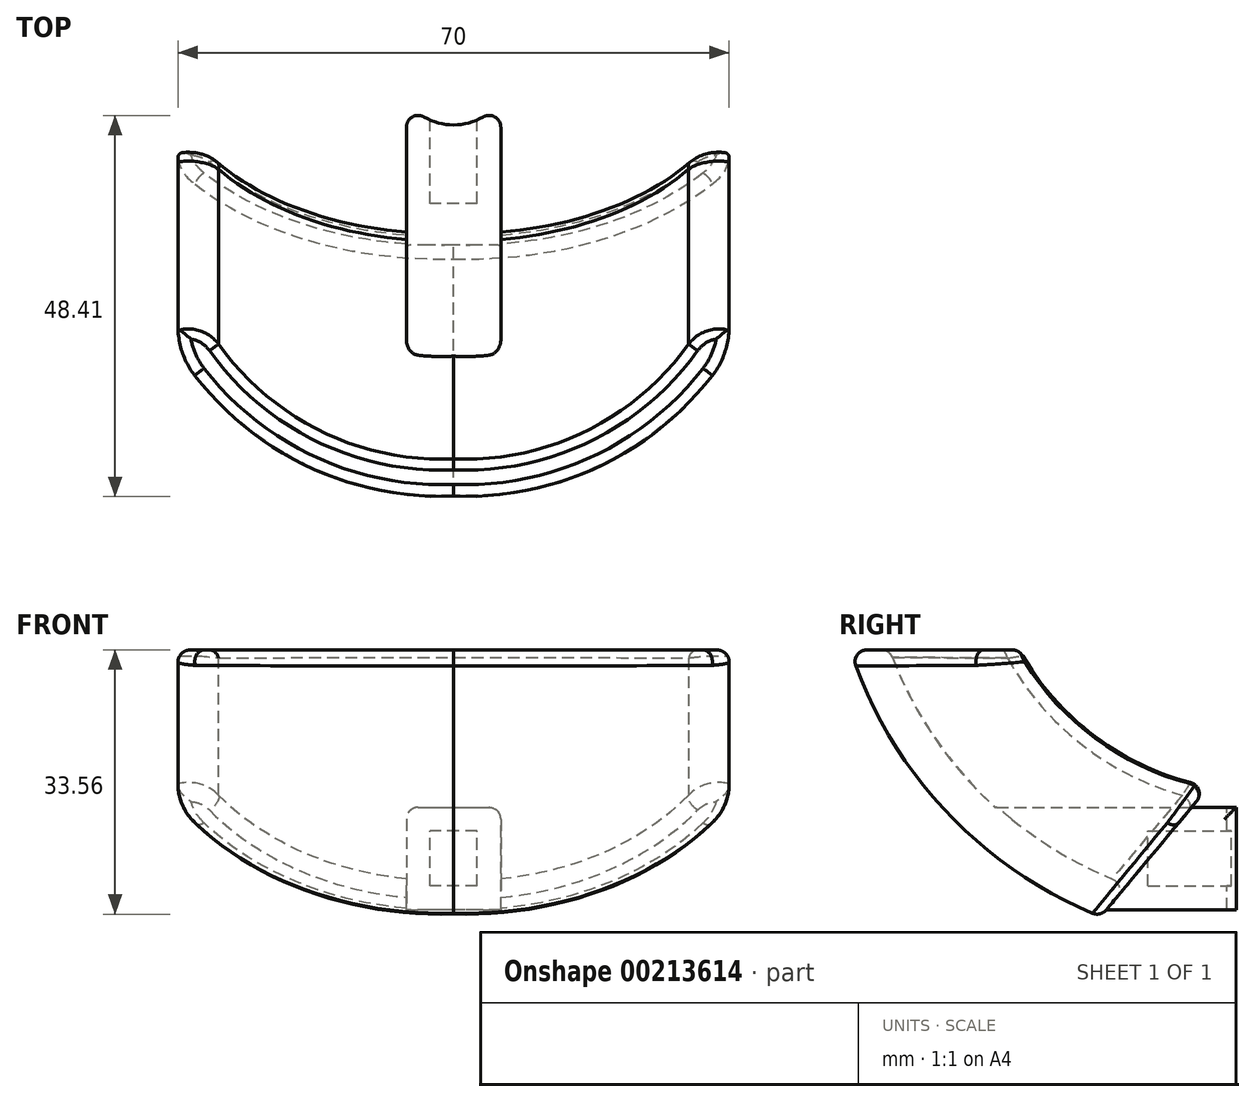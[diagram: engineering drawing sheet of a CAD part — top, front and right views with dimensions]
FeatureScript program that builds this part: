
annotation { "Feature Type Name" : "Feature", "Feature Type Description" : "" }
export const myFeature = defineFeature(function(context is Context, id is Id, definition is map)
    precondition{}
    {
        {
            var Q0;
            Q0=qCreatedBy(makeId("Right.planeOp"),FACE);
            var sketch = newSketch(context, id + "F0", { "sketchPlane" : qUnion([Q0])});
            skLineSegment(sketch, "E0.bottom", {"start": v(0, 0) * mm, "end": v(30, 0) * mm, "construction": true});
            skLineSegment(sketch, "E0.left", {"start": v(0, 0) * mm, "end": v(0, 30) * mm, "construction": true});
            skArc(sketch, "E1", {"start": v(0, 30) * mm, "mid": v(11.66, 11.66) * mm, "end": v(30, 0) * mm});
            skPoint(sketch, "E2", {"position": v(13.08, 10.3) * mm});
            skPoint(sketch, "E3", {"position": v(-15, 30) * mm});
            skPoint(sketch, "E4", {"position": v(3.08, 10.3) * mm});
            skPoint(sketch, "E5", {"position": v(30, 0) * mm});
            skPoint(sketch, "E6", {"position": v(25, 0) * mm});
            skFitSpline(sketch, "E7", {"points": [v(-15, 30) * mm, v(25, 0) * mm, v(100.66, 9.32) * mm], "startDerivative": vector(35.39, -77.1) * mm, "endDerivative": vector(150.07, 40.05) * mm});
            skSolve(sketch);
        }
        {
            var Q0;
            Q0=sQuery(id+"F0.wireOp",VERTEX,"E1.start");
            var Q1;
            Q1=qCreatedBy(makeId("Top.planeOp"),FACE);
            cPlane(context, id + "F1", {"entities" : qUnion([Q0, Q1]), "cplaneType" : CPlaneType.PLANE_POINT, "offset" : 25 * mm, "width" : 150 * mm, "height" : 150 * mm});
        }
        {
            var Q0;
            Q0=qCreatedBy(id+"F1.planeOp",FACE);
            var sketch = newSketch(context, id + "F2", { "sketchPlane" : qUnion([Q0])});
            skArc(sketch, "E8", {"start": v(-35, 24.67) * mm, "mid": v(-21.71, 6.36) * mm, "end": v(0, 0) * mm});
            skArc(sketch, "E9", {"start": v(0, 0) * mm, "mid": v(21.71, 6.36) * mm, "end": v(35, 24.67) * mm});
            skLineSegment(sketch, "E10", {"start": v(-35, 24.67) * mm, "end": v(-35, 16.25) * mm});
            skArc(sketch, "E11.0", {"start": v(0, -5) * mm, "mid": v(18.2, -1.4) * mm, "end": v(32.82, 10.02) * mm});
            skArc(sketch, "E11.1", {"start": v(-32.82, 10.02) * mm, "mid": v(-18.2, -1.4) * mm, "end": v(0, -5) * mm});
            skLineSegment(sketch, "E12", {"start": v(35, 24.67) * mm, "end": v(35, 16.25) * mm});
            skEllipticalArc(sketch, "E13", {});
            skPoint(sketch, "E14.visualSharp", {"position": v(-35, 13.03) * mm});
            skArc(sketch, "E14.filletArc", {"start": v(-35, 16.25) * mm, "mid": v(-34.44, 12.95) * mm, "end": v(-32.82, 10.02) * mm});
            skPoint(sketch, "E15.visualSharp", {"position": v(35, 13.03) * mm});
            skArc(sketch, "E15.filletArc", {"start": v(32.82, 10.02) * mm, "mid": v(34.44, 12.95) * mm, "end": v(35, 16.25) * mm});
            skEllipticalArc(sketch, "E16.trimOffspring", {});
            skPoint(sketch, "E17.orphan", {"position": v(0, -15) * mm});
            const initialGuessF2  = {"E13": [0, -0.005004295268239853, 0, -1, 0.01, 0.00424685629998106, 4.184836836168355, 4.7062911756630585], "E16.trimOffspring": [0, -0.005004295268239853, 0, -1, 0.01, 0.00424685629998106, 1.576894131516556, 2.098348471011326]};
            skSetInitialGuess(sketch, initialGuessF2);
            skSolve(sketch);
        }
        {
            var Q0;
            Q0=sQuery(id+"F0.wireOp",VERTEX,"E2");
            var Q1;
            Q1=qCreatedBy(makeId("Top.planeOp"),FACE);
            cPlane(context, id + "F3", {"entities" : qUnion([Q0, Q1]), "cplaneType" : CPlaneType.PLANE_POINT, "offset" : 25 * mm, "width" : 150 * mm, "height" : 150 * mm});
        }
        {
            var Q0;
            {var subQ5=sQuery(id+"F2.wireOp",EDGE,"E10");Q0=makeQuery(id+"F2.imprint","IMPRINT",FACE,{"disambiguationData":[TD([[makeQuery(id+"F2.imprint","IMPRINT",EDGE,{"derivedFrom":subQ5}),1.0]])]});}
            var Q1;
            {var subQ6=sQuery(id+"F2.wireOp",EDGE,"E9");var subQ7=sQuery(id+"F2.wireOp",EDGE,"E8");var subQ8=makeQuery(id+"F2.imprint","INTERSECT",VERTEX,{"derivedFrom":[subQ7,subQ6]});Q1=makeQuery(id+"F2.imprint","IMPRINT",FACE,{"disambiguationData":[TD([[makeQuery(id+"F2.imprint","IMPRINT",EDGE,{"disambiguationData":[TD([[subQ8,1.0]])],"derivedFrom":subQ7}),-1.0]])]});}
            var Q2;
            {var subQ5=sQuery(id+"F2.wireOp",EDGE,"E12");Q2=makeQuery(id+"F2.imprint","IMPRINT",FACE,{"disambiguationData":[TD([[makeQuery(id+"F2.imprint","IMPRINT",EDGE,{"derivedFrom":subQ5}),-1.0]])]});}
            var Q3;
            {var subQ0=sQuery(id+"F2.wireOp",EDGE,"lZaFmeEu-P24d-Nwwk-X734-4g5lw6kWDEKw");Q3=makeQuery(id+"F2.imprint","IMPRINT",FACE,{"disambiguationData":[TD([[makeQuery(id+"F2.imprint","IMPRINT",EDGE,{"derivedFrom":subQ0}),1.0]])]});}
            var Q4;
            {var subQ0=sQuery(id+"F2.wireOp",EDGE,"lZaFmeEu-P24d-Nwwk-X734-4g5lw6kWDEKw");Q4=makeQuery(id+"F2.imprint","IMPRINT",FACE,{"disambiguationData":[TD([[makeQuery(id+"F2.imprint","IMPRINT",EDGE,{"derivedFrom":subQ0}),-1.0]])]});}
            var Q5;
            Q5=sQuery(id+"F0.wireOp",EDGE,"E1");
            sweep(context, id + "F4", {"profiles" : qUnion([Q0, Q1, Q2, Q3, Q4]), "path" : qUnion([Q5])});
        }
        {
            var Q0;
            Q0=qCreatedBy(makeId("Front.planeOp"),FACE);
            var Q1;
            Q1=makeQuery(id+"F4.opSweep","CAP_VERTEX",VERTEX,{"disambiguationData":[OSD([sQuery(id+"F0.wireOp",EDGE,"E1"),sQuery(id+"F2.wireOp",EDGE,"E9"),sQuery(id+"F2.wireOp",EDGE,"E12")])],"isStart":false});
            cPlane(context, id + "F5", {"entities" : qUnion([Q0, Q1]), "cplaneType" : CPlaneType.PLANE_POINT, "offset" : 25 * mm, "width" : 150 * mm, "height" : 150 * mm});
        }
        {
            var Q0;
            Q0=qCreatedBy(id+"F5.planeOp",FACE);
            var sketch = newSketch(context, id + "F6", { "sketchPlane" : qUnion([Q0])});
            skLineSegment(sketch, "E18.bottom", {"start": v(3, 0) * mm, "end": v(-3, 0) * mm});
            skLineSegment(sketch, "E18.top", {"start": v(3, 7) * mm, "end": v(-3, 7) * mm});
            skLineSegment(sketch, "E18.left", {"start": v(3, 0) * mm, "end": v(3, 7) * mm});
            skLineSegment(sketch, "E18.right", {"start": v(-3, 0) * mm, "end": v(-3, 7) * mm});
            skPoint(sketch, "E18.middle", {"position": v(0, 3.5) * mm});
            skLineSegment(sketch, "E19.0", {"start": v(6, 10) * mm, "end": v(-6, 10) * mm});
            skLineSegment(sketch, "E19.1", {"start": v(6, -3) * mm, "end": v(6, 10) * mm});
            skLineSegment(sketch, "E19.2", {"start": v(6, -3) * mm, "end": v(-6, -3) * mm});
            skLineSegment(sketch, "E19.3", {"start": v(-6, -3) * mm, "end": v(-6, 10) * mm});
            skSolve(sketch);
        }
        {
            var Q0;
            Q0=makeQuery(id+"F6.imprint","IMPRINT",FACE,{"disambiguationData":[TD([[makeQuery(id+"F6.imprint","IMPRINT",EDGE,{"derivedFrom":sQuery(id+"F6.wireOp",EDGE,"E18.bottom")}),1.0]])]});
            var Q1;
            Q1=makeQuery(id+"F6.imprint","IMPRINT",FACE,{"disambiguationData":[TD([[makeQuery(id+"F6.imprint","IMPRINT",EDGE,{"derivedFrom":sQuery(id+"F6.wireOp",EDGE,"E18.bottom")}),-1.0]])]});
            extrude(context, id + "F7", {"entities" : qUnion([Q0, Q1]), "operationType" : NewBodyOperationType.ADD, "endBound" : BoundingType.UP_TO_NEXT, "depth" : 25 * mm});
        }
        {
            var Q0;
            Q0=makeQuery(id+"F6.imprint","IMPRINT",FACE,{"disambiguationData":[TD([[makeQuery(id+"F6.imprint","IMPRINT",EDGE,{"derivedFrom":sQuery(id+"F6.wireOp",EDGE,"E18.bottom")}),-1.0]])]});
            extrude(context, id + "F8", {"entities" : qUnion([Q0]), "operationType" : NewBodyOperationType.REMOVE, "depth" : 13 * mm});
        }
        {
            var Q0;
            Q0=makeQuery(id+"F7.opExtrude","SWEPT_FACE",FACE,{"disambiguationData":[OSD([sQuery(id+"F6.wireOp",EDGE,"E19.0")])]});
            var sketch = newSketch(context, id + "F9", { "sketchPlane" : qUnion([Q0])});
            skArc(sketch, "E20", {"start": v(-6, 45.79) * mm, "mid": v(0, 42.79) * mm, "end": v(6, 45.79) * mm});
            skLineSegment(sketch, "E21", {"start": v(-6, 45.79) * mm, "end": v(6, 45.79) * mm});
            skSolve(sketch);
        }
        {
            var Q0;
            Q0=qSketchRegion(id+"F9",true);
            extrude(context, id + "F10", {"entities" : qUnion([Q0]), "operationType" : NewBodyOperationType.REMOVE, "endBound" : BoundingType.THROUGH_ALL, "oppositeDirection" : true, "depth" : 25 * mm});
        }
        {
            var Q0;
            Q0=makeQuery(id+"F4.opSweep","SWEPT_EDGE",EDGE,{"disambiguationData":[OSD([sQuery(id+"F0.wireOp",EDGE,"E1"),sQuery(id+"F2.wireOp",EDGE,"E8"),sQuery(id+"F2.wireOp",EDGE,"E10")])]});
            var Q1;
            Q1=makeQuery(id+"F4.opSweep","SWEPT_EDGE",EDGE,{"disambiguationData":[OSD([sQuery(id+"F0.wireOp",EDGE,"E1"),sQuery(id+"F2.wireOp",EDGE,"E9"),sQuery(id+"F2.wireOp",EDGE,"E12")])]});
            fillet(context, id + "F11", {"entities" : qUnion([Q0, Q1]), "radius" : 5 * mm, "tangentPropagation" : true, "allowEdgeOverflow" : false});
        }
        {
            var Q0;
            Q0=makeQuery(id+"F4.opSweep","CAP_EDGE",EDGE,{"disambiguationData":[OSD([sQuery(id+"F0.wireOp",VERTEX,"E1.start"),sQuery(id+"F2.wireOp",EDGE,"E11.0")])],"isStart":true});
            var Q1;
            Q1=makeQuery(id+"F4.opSweep","CAP_EDGE",EDGE,{"disambiguationData":[OSD([sQuery(id+"F0.wireOp",VERTEX,"E1.start"),sQuery(id+"F2.wireOp",EDGE,"E11.1")])],"isStart":true});
            var Q2;
            Q2=makeQuery(id+"F4.opSweep","CAP_EDGE",EDGE,{"disambiguationData":[OSD([sQuery(id+"F0.wireOp",VERTEX,"E1.end"),sQuery(id+"F2.wireOp",EDGE,"E11.0")])],"isStart":false});
            var Q3;
            Q3=makeQuery(id+"F4.opSweep","CAP_EDGE",EDGE,{"disambiguationData":[OSD([sQuery(id+"F0.wireOp",VERTEX,"E1.end"),sQuery(id+"F2.wireOp",EDGE,"E11.1")])],"isStart":false});
            var Q4;
            Q4=makeQuery(id+"F4.opSweep","CAP_EDGE",EDGE,{"disambiguationData":[OSD([sQuery(id+"F0.wireOp",VERTEX,"E1.end"),sQuery(id+"F2.wireOp",EDGE,"E9")])],"isStart":false});
            var Q5;
            Q5=makeQuery(id+"F4.opSweep","CAP_EDGE",EDGE,{"disambiguationData":[OSD([sQuery(id+"F0.wireOp",VERTEX,"E1.end"),sQuery(id+"F2.wireOp",EDGE,"E8")])],"isStart":false});
            var Q6;
            Q6=makeQuery(id+"F4.opSweep","CAP_EDGE",EDGE,{"disambiguationData":[OSD([sQuery(id+"F0.wireOp",VERTEX,"E1.start"),sQuery(id+"F2.wireOp",EDGE,"E8")])],"isStart":true});
            var Q7;
            {var subQ0=sQuery(id+"F2.wireOp",EDGE,"E12");var subQ1=sQuery(id+"F2.wireOp",EDGE,"E9");Q7=makeQuery(id+"F11.opFillet","BLEND_EDGE",EDGE,{"blendedFrom":[makeQuery(id+"F4.opSweep","SWEPT_EDGE",EDGE,{"disambiguationData":[OSD([sQuery(id+"F0.wireOp",EDGE,"E1"),subQ1,subQ0])]}),makeQuery(id+"F4.opSweep","CAP_FACE",FACE,{"disambiguationData":[OSD([sQuery(id+"F0.wireOp",VERTEX,"E1.start"),sQuery(id+"F2.wireOp",EDGE,"E8"),subQ1,sQuery(id+"F2.wireOp",EDGE,"E10"),sQuery(id+"F2.wireOp",EDGE,"E11.0"),sQuery(id+"F2.wireOp",EDGE,"E11.1"),subQ0,sQuery(id+"F2.wireOp",EDGE,"E14.filletArc"),sQuery(id+"F2.wireOp",EDGE,"E15.filletArc")])],"isStart":true})],"blendedInto":[makeQuery(id+"F4.opSweep","CAP_FACE",FACE,{"disambiguationData":[OSD([sQuery(id+"F0.wireOp",VERTEX,"E1.start"),sQuery(id+"F2.wireOp",EDGE,"E8"),subQ1,sQuery(id+"F2.wireOp",EDGE,"E10"),sQuery(id+"F2.wireOp",EDGE,"E11.0"),sQuery(id+"F2.wireOp",EDGE,"E11.1"),subQ0,sQuery(id+"F2.wireOp",EDGE,"E14.filletArc"),sQuery(id+"F2.wireOp",EDGE,"E15.filletArc")])],"isStart":true})]});}
            var Q8;
            Q8=makeQuery(id+"F7.opExtrude","SWEPT_EDGE",EDGE,{"disambiguationData":[OSD([sQuery(id+"F6.wireOp",EDGE,"E19.0"),sQuery(id+"F6.wireOp",EDGE,"E19.1")])]});
            var Q9;
            Q9=makeQuery(id+"F7.opExtrude","SWEPT_EDGE",EDGE,{"disambiguationData":[OSD([sQuery(id+"F6.wireOp",EDGE,"E19.0"),sQuery(id+"F6.wireOp",EDGE,"E19.3")])]});
            var Q10;
            {var subQ0=sQuery(id+"F6.wireOp",EDGE,"E19.1");Q10=makeQuery(id+"F10.boolean.opBoolean","MERGE",EDGE,{"derivedFrom":[makeQuery(id+"F7.opExtrude","CAP_EDGE",EDGE,{"disambiguationData":[OSD([subQ0])],"isStart":true}),makeQuery(id+"F10.opExtrude","SWEPT_EDGE",EDGE,{"disambiguationData":[OSD([sQuery(id+"F6.wireOp",EDGE,"E19.0"),subQ0,sQuery(id+"F9.wireOp",EDGE,"E20"),sQuery(id+"F9.wireOp",EDGE,"E21")])]})]});}
            var Q11;
            {var subQ0=sQuery(id+"F6.wireOp",EDGE,"E19.3");Q11=makeQuery(id+"F10.boolean.opBoolean","MERGE",EDGE,{"derivedFrom":[makeQuery(id+"F7.opExtrude","CAP_EDGE",EDGE,{"disambiguationData":[OSD([subQ0])],"isStart":true}),makeQuery(id+"F10.opExtrude","SWEPT_EDGE",EDGE,{"disambiguationData":[OSD([sQuery(id+"F6.wireOp",EDGE,"E19.0"),subQ0,sQuery(id+"F9.wireOp",EDGE,"E20"),sQuery(id+"F9.wireOp",EDGE,"E21")])]})]});}
            fillet(context, id + "F12", {"entities" : qUnion([Q0, Q1, Q2, Q3, Q4, Q5, Q6, Q7, Q8, Q9, Q10, Q11]), "radius" : 1.5 * mm, "tangentPropagation" : true, "allowEdgeOverflow" : false});
        }
    });
